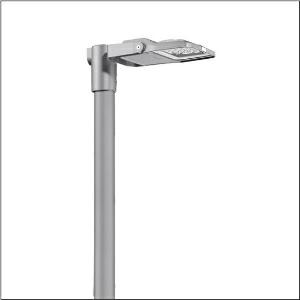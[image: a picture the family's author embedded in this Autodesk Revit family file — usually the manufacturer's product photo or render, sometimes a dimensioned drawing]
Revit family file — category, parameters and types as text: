
# Revit family: floodlight_fl_21_iq_micro___pl61_5xa7762a2c3a_d37b
name_source: partatom
category: Lighting Fixtures
units: mm (PartAtom-declared; Revit-internal decimal feet)

## family parameters
Cut with Voids When Loaded = No
Host = Face
Light Source = No
Part Type = Normal
Room Calculation Point = No
Round Connector Dimension = Use Diameter
Shared = No

## types (1)
- --- (1 x LED, 2910 lm, 23.1 W, 3000K)
    Apparent Load = 23 VA
    CIE Flux Codes = 33 65 98 100 100
    Color Rendering = 70
    Color Temperature = 3000K
    Default Elevation = 1800 mm
    Description = Floodlight FL 21 iQ micro, floodlight, primary light control with lens, of PMMA, primary optical cover: protective disc, of toughened safety glass, transparent, light distribution: PL61, light emission: direct distribution, installation type: surface-mounted, LED, High Power LED, rated luminous flux: 2.910lm, luminous efficacy: 126lm/W, light colour: 730, colour temperature: 3000K, control: Auto-Match, Temp-Guard, Night-Set, Smart-Wire, Desk-Remote (wireless, voltage-free reading and setting of iQ features in the workshop via application-optimized NFC function/RFID function), optimised constant luminous flux control (CLO 2.0), Street-Remote, with terminal, 6-pole, mains connection: 220..240V, AC, 50/60Hz, start of lifetime: 23W, end of service life: 24W, reduction: 11W, luminaire housing, of diecast aluminium, powder-coated, Siteco® metallic grey (DB 702S), corrosivity category C5 mid according to DIN EN ISO 12944, sealing non-destructively replaceable, please order mast flange separately, mast bracket, of steel, galvanised, powder-coated, Siteco® metallic grey (DB 702S), protection rating (complete): IP66, insulation class (complete): insulation class II (safety insulation), certification: CE, ENEC, VDE, protection symbol: D, impact resistance: IK07, permissible operating ambient temperature: -40..+40°C, permissible operating ambient temperature for outdoor applications: -40..+50°C, standard: DIN EN 12944, LABS conformity tested according to VDMA 24364:2018-05, packaging unit: 1 piece

Light Distribution: PL61
    Height = 65 mm
    Lamp = 1 x LED
    Lamp Light Flux = 2910 lm
    Lamp Power = 23.1 W
    Lamp count = 1
    Length = 312 mm
    Luminous efficacy = 126 lm/W
    Manufacturer = Siteco
    ModVariant = No
    Model = 5XA7762A2C3A
    Number of Poles = 1
    OnlyDefault = Yes
    Power Factor = 1
    Product Name = Floodlight FL 21 iQ micro | PL61
    Product group = floodlight | pylon annexe
    ProductGroupID = 6200
    Protection Class = Protection class II
    Protection Degree = IP 66
    RLX_Detail_Level = 1
    RLX_Emergency_Light_Flux = 0 lm
    RLX_Emergency_Type = 0
    RLX_Emergency_Type_DB = No
    RlxData = <blob elided: 101857 chars, md5=4789ee58>
    Socket = socket
    Standby Power = 0 W
    System Light Flux = 2910 lm
    System Power = 23 W
    Type Comments = factory setting: luminous flux: 100 % | dim-lin: 254 | 455 mA
    Type Image = l_1007121.jpg
    URL = http://relux.com
    VarID = @adj_128875
    Voltage = 0 V
    Weight = 0.00 kg
    Width = 230 mm

## geometry (parser evidence)
native form markers: Blend x4, Sweep x10
no freeform markers — native parametric forms only
